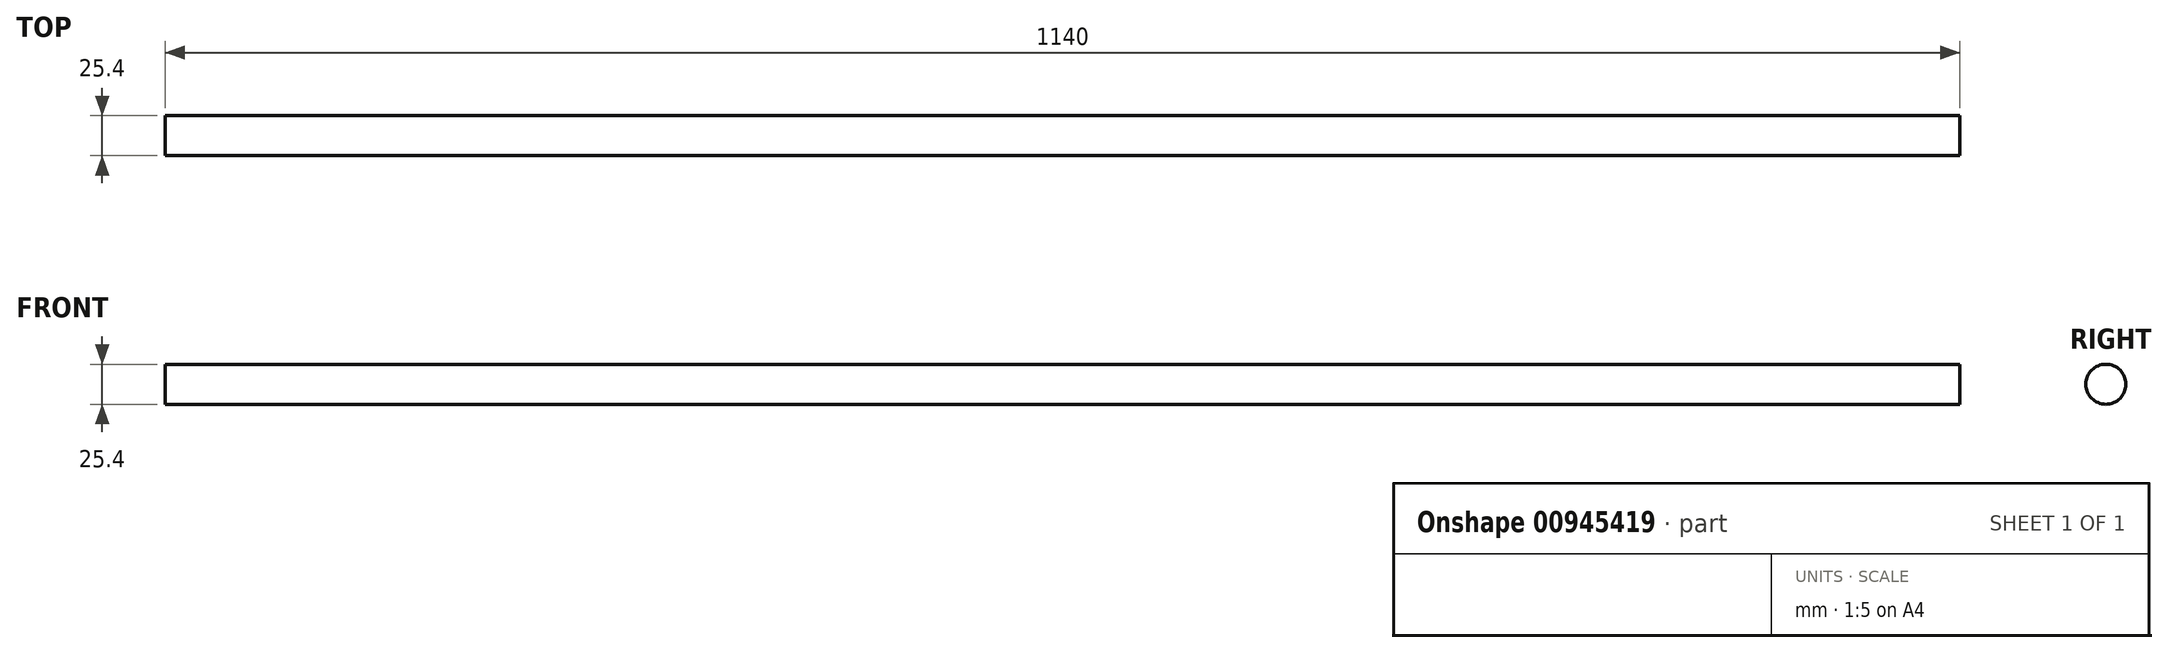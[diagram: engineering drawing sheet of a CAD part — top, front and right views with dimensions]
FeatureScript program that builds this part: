
annotation { "Feature Type Name" : "Feature", "Feature Type Description" : "" }
export const myFeature = defineFeature(function(context is Context, id is Id, definition is map)
    precondition{}
    {
        {
            var Q0;
            Q0=qCreatedBy(makeId("Right.planeOp"),FACE);
            var sketch = newSketch(context, id + "F0", { "sketchPlane" : qUnion([Q0])});
            skCircle(sketch, "E0", {"center": v(0, 0) * mm, "radius": 12.7 * mm});
            skSolve(sketch);
        }
        {
            var Q0;
            Q0=sQuery(id+"F0.wireOp",EDGE,"E0");
            extrude(context, id + "F1", {"bodyType" : ToolBodyType.SURFACE, "surfaceEntities" : qUnion([Q0]), "depth" : 1140 * mm, "offsetDistance" : 25.4 * mm});
        }
    });
